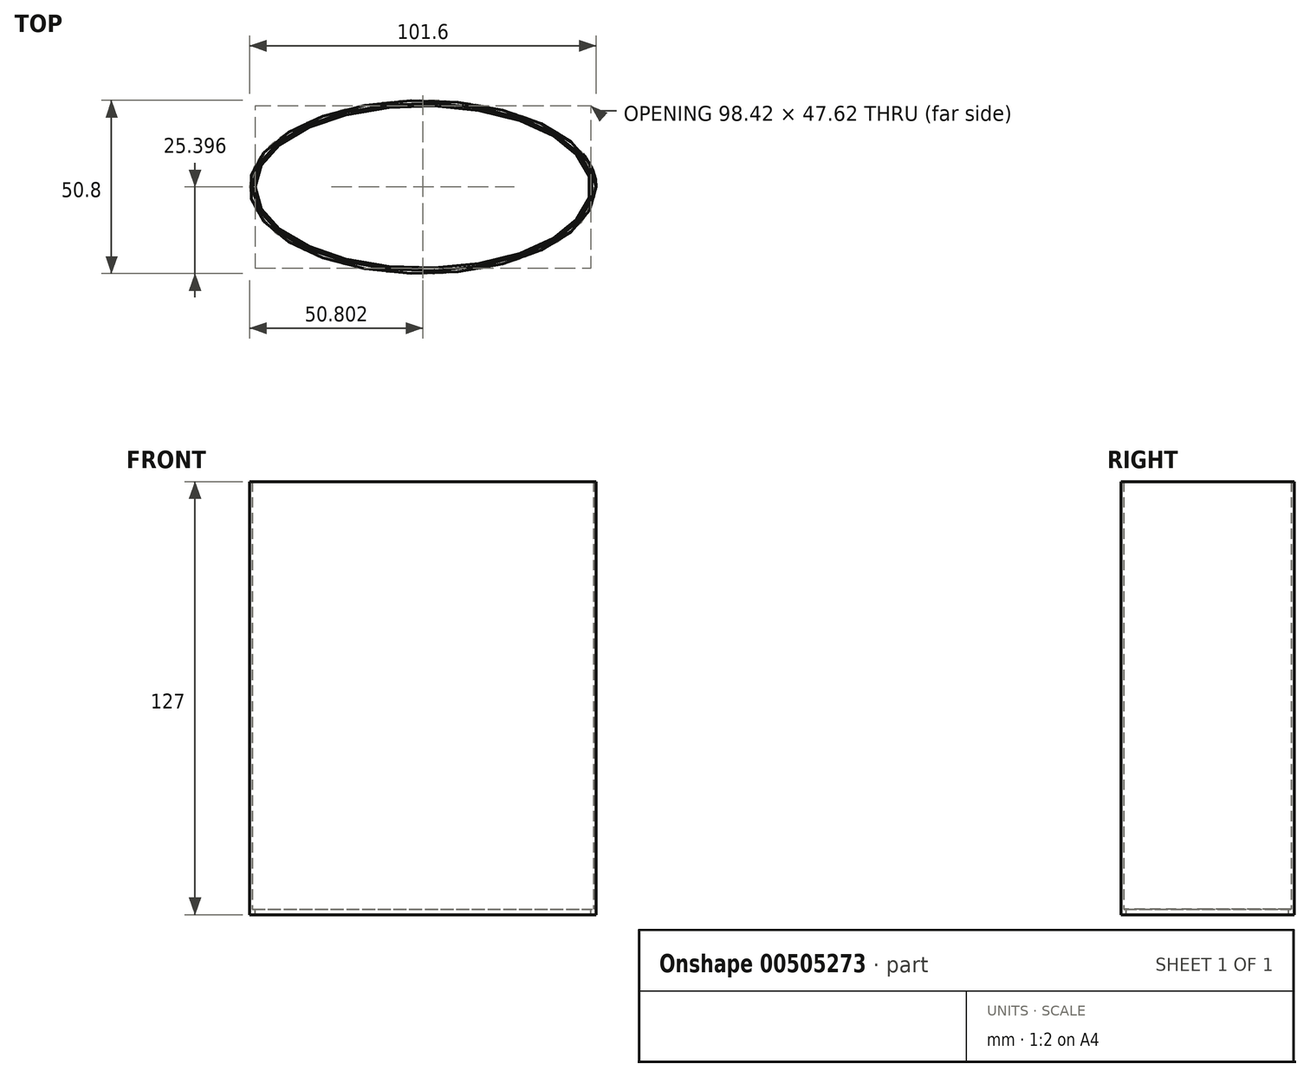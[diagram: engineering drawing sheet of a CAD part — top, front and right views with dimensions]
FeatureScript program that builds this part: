
annotation { "Feature Type Name" : "Feature", "Feature Type Description" : "" }
export const myFeature = defineFeature(function(context is Context, id is Id, definition is map)
    precondition{}
    {
        {
            var Q0;
            Q0=qCreatedBy(makeId("Top.planeOp"),FACE);
            var sketch = newSketch(context, id + "F0", { "sketchPlane" : qUnion([Q0])});
            skEllipse(sketch, "E0", {"center": v(-27.15, 12.26) * mm, "majorRadius": 50.8 * mm, "minorRadius": 25.4 * mm, "majorAxis": v(1, 0)});
            skEllipse(sketch, "E1", {"center": v(-27.15, 12.26) * mm, "majorRadius": 50 * mm, "minorRadius": 24.6 * mm, "majorAxis": v(-1, 0)});
            skSolve(sketch);
        }
        {
            var Q0;
            Q0=makeQuery(id+"F0.imprint","IMPRINT",FACE,{"disambiguationData":[TD([[makeQuery(id+"F0.imprint","IMPRINT",EDGE,{"derivedFrom":sQuery(id+"F0.wireOp",EDGE,"E0")}),1.0]])]});
            extrude(context, id + "F1", {"entities" : qUnion([Q0]), "depth" : 125.4 * mm});
        }
        {
            var Q0;
            Q0=qCreatedBy(makeId("Top.planeOp"),FACE);
            var sketch = newSketch(context, id + "F2", { "sketchPlane" : qUnion([Q0])});
            skEllipse(sketch, "E2", {"center": v(-27.15, 12.26) * mm, "majorRadius": 50.8 * mm, "minorRadius": 25.4 * mm, "majorAxis": v(-1, 0)});
            skEllipse(sketch, "E3", {"center": v(-27.15, 12.26) * mm, "majorRadius": 49.21 * mm, "minorRadius": 23.81 * mm, "majorAxis": v(-1, 0)});
            skSolve(sketch);
        }
        {
            var Q0;
            Q0=makeQuery(id+"F2.imprint","IMPRINT",FACE,{"disambiguationData":[TD([[makeQuery(id+"F2.imprint","IMPRINT",EDGE,{"derivedFrom":sQuery(id+"F2.wireOp",EDGE,"E2")}),1.0]])]});
            extrude(context, id + "F3", {"entities" : qUnion([Q0]), "operationType" : NewBodyOperationType.ADD, "depth" : -1.59 * mm});
        }
    });
